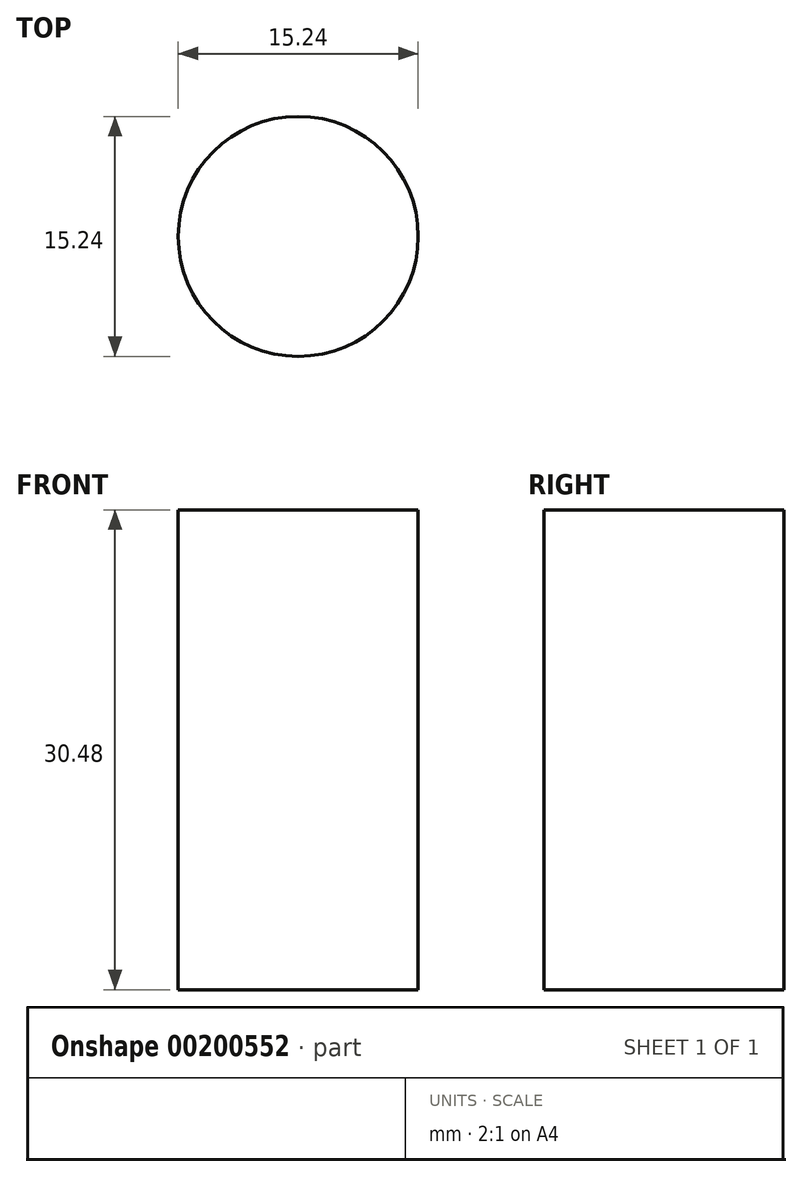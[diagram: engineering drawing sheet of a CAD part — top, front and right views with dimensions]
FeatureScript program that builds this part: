
annotation { "Feature Type Name" : "Feature", "Feature Type Description" : "" }
export const myFeature = defineFeature(function(context is Context, id is Id, definition is map)
    precondition{}
    {
        {
            var Q0;
            Q0=qCreatedBy(makeId("Top.planeOp"),FACE);
            var sketch = newSketch(context, id + "F0", { "sketchPlane" : qUnion([Q0])});
            skLineSegment(sketch, "E0", {"start": v(-32.13, 0) * mm, "end": v(0, 0) * mm});
            skCircle(sketch, "E1", {"center": v(-36.14, -14.76) * mm, "radius": 7.62 * mm});
            skSolve(sketch);
        }
        {
            var Q0;
            Q0=makeQuery(id+"F0.imprint","IMPRINT",FACE,{"disambiguationData":[TD([[makeQuery(id+"F0.imprint","IMPRINT",EDGE,{"derivedFrom":sQuery(id+"F0.wireOp",EDGE,"E1")}),1.0]])]});
            extrude(context, id + "F1", {"entities" : qUnion([Q0]), "depth" : 30.48 * mm});
        }
    });
